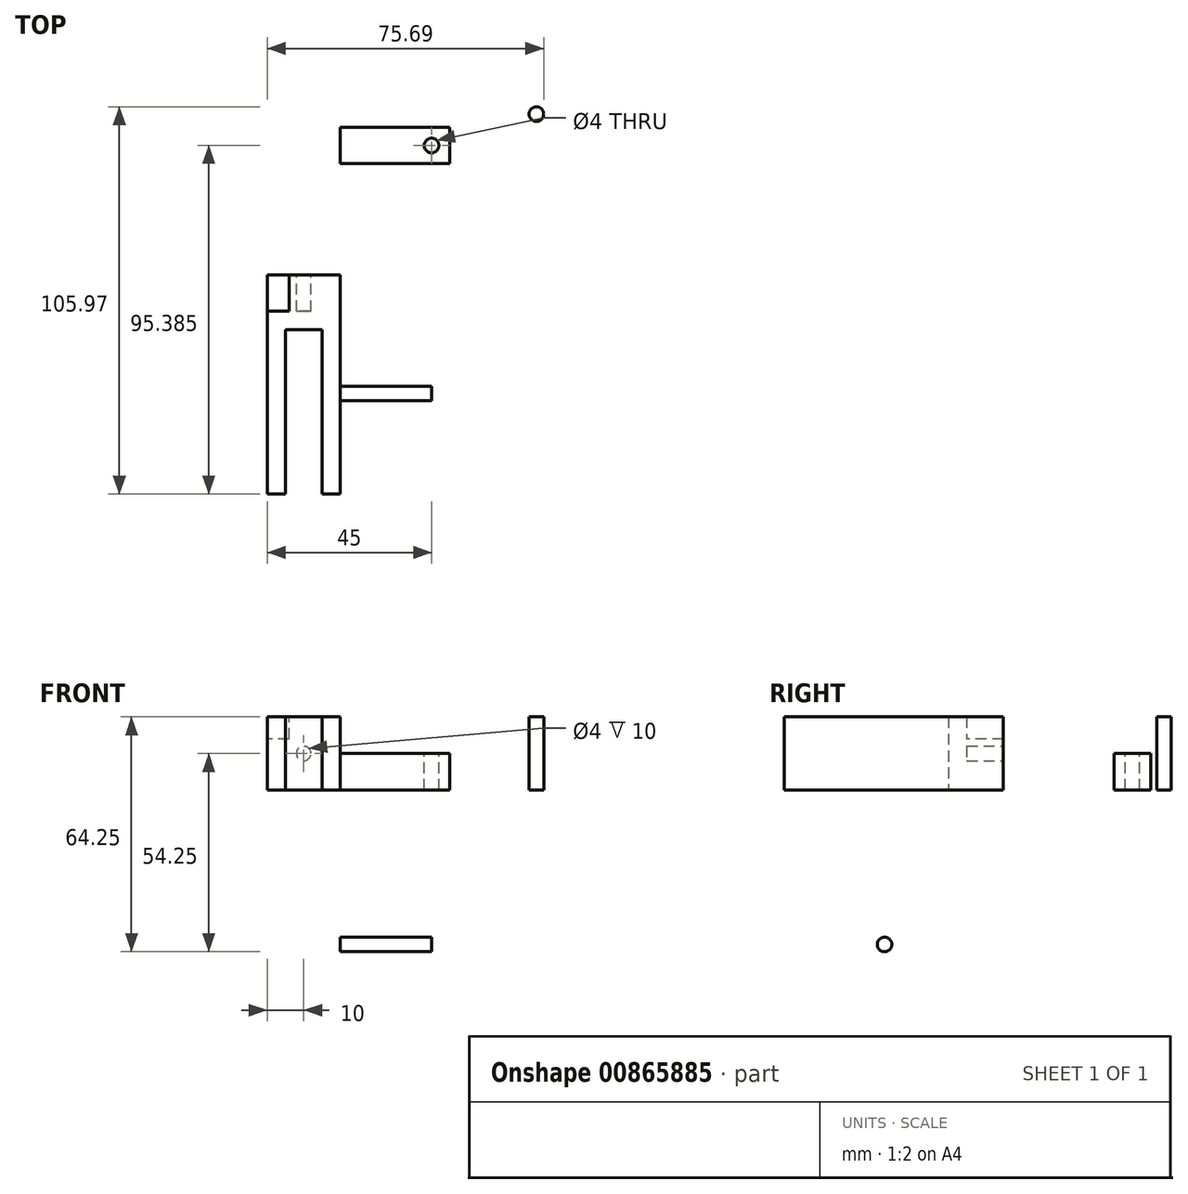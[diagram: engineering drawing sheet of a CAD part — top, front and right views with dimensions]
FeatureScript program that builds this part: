
annotation { "Feature Type Name" : "Feature", "Feature Type Description" : "" }
export const myFeature = defineFeature(function(context is Context, id is Id, definition is map)
    precondition{}
    {
        {
            var Q0;
            Q0=qCreatedBy(makeId("Front.planeOp"),FACE);
            var sketch = newSketch(context, id + "F0", { "sketchPlane" : qUnion([Q0])});
            skLineSegment(sketch, "E0.bottom", {"start": v(0, 0) * mm, "end": v(-20, 0) * mm});
            skLineSegment(sketch, "E0.top", {"start": v(0, 20) * mm, "end": v(-20, 20) * mm});
            skLineSegment(sketch, "E0.left", {"start": v(0, 0) * mm, "end": v(0, 20) * mm});
            skLineSegment(sketch, "E0.right", {"start": v(-20, 0) * mm, "end": v(-20, 20) * mm});
            skSolve(sketch);
        }
        {
            var Q0;
            Q0 = qSketchRegion(id + "F0", true);
            extrude(context, id + "F1", {"entities" : qUnion([Q0]), "depth" : 60 * mm, "offsetDistance" : 25 * mm});
        }
        {
            var Q0;
            Q0=makeQuery(id+"F1.opExtrude","CAP_FACE",FACE,{"disambiguationData":[OSD([sQuery(id+"F0.wireOp",EDGE,"E0.bottom"),sQuery(id+"F0.wireOp",EDGE,"E0.top"),sQuery(id+"F0.wireOp",EDGE,"E0.left"),sQuery(id+"F0.wireOp",EDGE,"E0.right")])],"isStart":false});
            var sketch = newSketch(context, id + "F2", { "sketchPlane" : qUnion([Q0])});
            skLineSegment(sketch, "E1.bottom", {"start": v(-15, 20) * mm, "end": v(-5, 20) * mm});
            skLineSegment(sketch, "E1.top", {"start": v(-15, 0) * mm, "end": v(-5, 0) * mm});
            skLineSegment(sketch, "E1.left", {"start": v(-15, 20) * mm, "end": v(-15, 0) * mm});
            skLineSegment(sketch, "E1.right", {"start": v(-5, 20) * mm, "end": v(-5, 0) * mm});
            skSolve(sketch);
        }
        {
            var Q0;
            Q0 = qSketchRegion(id + "F2", true);
            extrude(context, id + "F3", {"entities" : qUnion([Q0]), "operationType" : NewBodyOperationType.REMOVE, "oppositeDirection" : true, "depth" : 45 * mm, "offsetDistance" : 25 * mm});
        }
        {
            var Q0;
            Q0=qCreatedBy(makeId("Right.planeOp"),FACE);
            var sketch = newSketch(context, id + "F4", { "sketchPlane" : qUnion([Q0])});
            skLineSegment(sketch, "E2.bottom", {"start": v(40.38, 0) * mm, "end": v(30.38, 0) * mm});
            skLineSegment(sketch, "E2.top", {"start": v(40.38, 10) * mm, "end": v(30.38, 10) * mm});
            skLineSegment(sketch, "E2.left", {"start": v(40.38, 0) * mm, "end": v(40.38, 10) * mm});
            skLineSegment(sketch, "E2.right", {"start": v(30.38, 0) * mm, "end": v(30.38, 10) * mm});
            skSolve(sketch);
        }
        {
            var Q0;
            Q0 = qSketchRegion(id + "F4", true);
            extrude(context, id + "F5", {"entities" : qUnion([Q0]), "depth" : 30 * mm, "offsetDistance" : 25 * mm});
        }
        {
            var Q0;
            Q0=makeQuery(id+"F5.opExtrude","SWEPT_FACE",FACE,{"disambiguationData":[OSD([sQuery(id+"F4.wireOp",EDGE,"E2.top")])]});
            var sketch = newSketch(context, id + "F6", { "sketchPlane" : qUnion([Q0])});
            skCircle(sketch, "E3", {"center": v(25, 35.38) * mm, "radius": 2 * mm});
            skSolve(sketch);
        }
        {
            var Q0;
            Q0 = qSketchRegion(id + "F6", true);
            extrude(context, id + "F7", {"entities" : qUnion([Q0]), "operationType" : NewBodyOperationType.REMOVE, "endBound" : BoundingType.THROUGH_ALL, "oppositeDirection" : true, "depth" : 5 * mm, "offsetDistance" : 25 * mm});
        }
        {
            var Q0;
            Q0=qCreatedBy(makeId("Right.planeOp"),FACE);
            var sketch = newSketch(context, id + "F8", { "sketchPlane" : qUnion([Q0])});
            skCircle(sketch, "E4", {"center": v(-32.48, -42.25) * mm, "radius": 2 * mm});
            skSolve(sketch);
        }
        {
            var Q0;
            Q0 = qSketchRegion(id + "F8", true);
            extrude(context, id + "F9", {"entities" : qUnion([Q0]), "depth" : 25 * mm, "offsetDistance" : 25 * mm});
        }
        {
            var Q0;
            Q0=makeQuery(id+"F1.opExtrude","CAP_FACE",FACE,{"disambiguationData":[OSD([sQuery(id+"F0.wireOp",EDGE,"E0.bottom"),sQuery(id+"F0.wireOp",EDGE,"E0.top"),sQuery(id+"F0.wireOp",EDGE,"E0.left"),sQuery(id+"F0.wireOp",EDGE,"E0.right")])],"isStart":true});
            var sketch = newSketch(context, id + "F10", { "sketchPlane" : qUnion([Q0])});
            skCircle(sketch, "E5", {"center": v(10, 10) * mm, "radius": 2 * mm});
            skPoint(sketch, "E5.centerSnap0", {"position": v(10, 20) * mm});
            skSolve(sketch);
        }
        {
            var Q0;
            Q0 = qSketchRegion(id + "F10", true);
            extrude(context, id + "F11", {"entities" : qUnion([Q0]), "operationType" : NewBodyOperationType.REMOVE, "oppositeDirection" : true, "depth" : 10 * mm, "offsetDistance" : 25 * mm});
        }
        {
            var Q0;
            Q0=makeQuery(id+"F1.opExtrude","SWEPT_FACE",FACE,{"disambiguationData":[OSD([sQuery(id+"F0.wireOp",EDGE,"E0.right")])]});
            var sketch = newSketch(context, id + "F12", { "sketchPlane" : qUnion([Q0])});
            skLineSegment(sketch, "E6.bottom", {"start": v(0, 20) * mm, "end": v(10, 20) * mm});
            skLineSegment(sketch, "E6.top", {"start": v(0, 14) * mm, "end": v(10, 14) * mm});
            skLineSegment(sketch, "E6.left", {"start": v(0, 20) * mm, "end": v(0, 14) * mm});
            skLineSegment(sketch, "E6.right", {"start": v(10, 20) * mm, "end": v(10, 14) * mm});
            skSolve(sketch);
        }
        {
            var Q0;
            Q0 = qSketchRegion(id + "F12", true);
            extrude(context, id + "F13", {"entities" : qUnion([Q0]), "operationType" : NewBodyOperationType.REMOVE, "oppositeDirection" : true, "depth" : 6 * mm, "offsetDistance" : 25 * mm});
        }
        {
            var Q0;
            Q0=qCreatedBy(makeId("Top.planeOp"),FACE);
            var sketch = newSketch(context, id + "F14", { "sketchPlane" : qUnion([Q0])});
            skCircle(sketch, "E7", {"center": v(53.69, 43.97) * mm, "radius": 2 * mm});
            skSolve(sketch);
        }
        {
            var Q0;
            Q0 = qSketchRegion(id + "F14", true);
            extrude(context, id + "F15", {"entities" : qUnion([Q0]), "depth" : 20 * mm, "offsetDistance" : 25 * mm});
        }
    });
